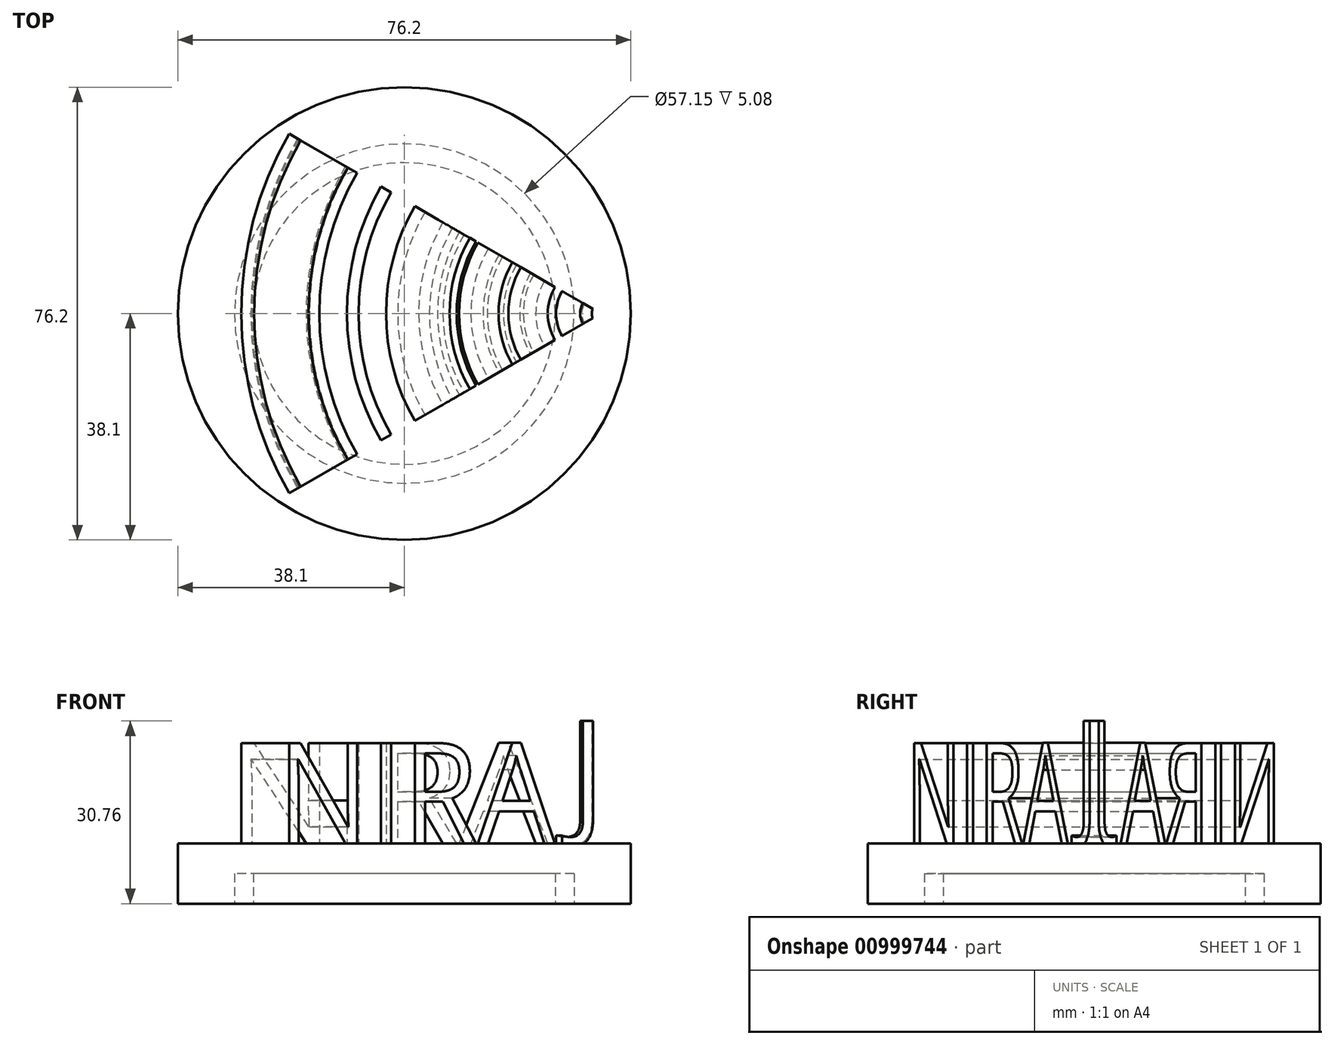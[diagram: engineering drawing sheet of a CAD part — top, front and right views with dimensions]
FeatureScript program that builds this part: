
annotation { "Feature Type Name" : "Feature", "Feature Type Description" : "" }
export const myFeature = defineFeature(function(context is Context, id is Id, definition is map)
    precondition{}
    {
        {
            var Q0;
            Q0=qCreatedBy(makeId("Top.planeOp"),FACE);
            var sketch = newSketch(context, id + "F0", { "sketchPlane" : qUnion([Q0])});
            skCircle(sketch, "E0", {"center": v(0, 0) * mm, "radius": 25.4 * mm});
            skCircle(sketch, "E1", {"center": v(0, 0) * mm, "radius": 28.58 * mm});
            skCircle(sketch, "E2", {"center": v(0, 0) * mm, "radius": 38.1 * mm});
            skSolve(sketch);
        }
        {
            var Q0;
            Q0=makeQuery(id+"F0.imprint","IMPRINT",FACE,{"disambiguationData":[TD([[makeQuery(id+"F0.imprint","IMPRINT",EDGE,{"derivedFrom":sQuery(id+"F0.wireOp",EDGE,"E1")}),-1.0]])]});
            var Q1;
            Q1=makeQuery(id+"F0.imprint","IMPRINT",FACE,{"disambiguationData":[TD([[makeQuery(id+"F0.imprint","IMPRINT",EDGE,{"derivedFrom":sQuery(id+"F0.wireOp",EDGE,"E0")}),-1.0]])]});
            var Q2;
            Q2=makeQuery(id+"F0.imprint","IMPRINT",FACE,{"disambiguationData":[TD([[makeQuery(id+"F0.imprint","IMPRINT",EDGE,{"derivedFrom":sQuery(id+"F0.wireOp",EDGE,"E0")}),1.0]])]});
            extrude(context, id + "F1", {"entities" : qUnion([Q0, Q1, Q2]), "depth" : 10.16 * mm, "offsetDistance" : 25.4 * mm});
        }
        {
            var Q0;
            Q0=makeQuery(id+"F0.imprint","IMPRINT",FACE,{"disambiguationData":[TD([[makeQuery(id+"F0.imprint","IMPRINT",EDGE,{"derivedFrom":sQuery(id+"F0.wireOp",EDGE,"E0")}),-1.0]])]});
            extrude(context, id + "F2", {"entities" : qUnion([Q0]), "operationType" : NewBodyOperationType.REMOVE, "depth" : 5.08 * mm, "offsetDistance" : 25.4 * mm});
        }
        {
            var Q0;
            Q0=qCreatedBy(makeId("Front.planeOp"),FACE);
            var sketch = newSketch(context, id + "F3", { "sketchPlane" : qUnion([Q0])});
            skText(sketch, "E3", { "text": "NIRAJ", "fontName": "OpenSans-Regular.ttf"});
            const initialGuessF3  = {"E3": [-0.02978, 0.01016, 1, 0, 0.017]};
            skSetInitialGuess(sketch, initialGuessF3);
            skSolve(sketch);
        }
        {
            var Q0;
            Q0=qCreatedBy(makeId("Front.planeOp"),FACE);
            var sketch = newSketch(context, id + "F4", { "sketchPlane" : qUnion([Q0])});
            skText(sketch, "E4", { "text": "NIRAJ", "fontName": "OpenSans-Regular.ttf"});
            const initialGuessF4  = {"E4": [-0.02654, 0.0139, 1, 0, 0.017]};
            skSetInitialGuess(sketch, initialGuessF4);
            skSolve(sketch);
        }
        {
            var Q0;
            Q0=makeQuery(id+"F3.imprint","IMPRINT",FACE,{"disambiguationData":[TD([[makeQuery(id+"F3.imprint","IMPRINT",EDGE,{"derivedFrom":sQuery(id+"F3.wireOp",EDGE,"E3.sketch_text.stroke-0")}),-1.0]])]});
            var Q1;
            Q1=makeQuery(id+"F3.imprint","IMPRINT",FACE,{"disambiguationData":[TD([[makeQuery(id+"F3.imprint","IMPRINT",EDGE,{"derivedFrom":sQuery(id+"F3.wireOp",EDGE,"E3.sketch_text.stroke-15")}),-1.0]])]});
            var Q2;
            Q2=makeQuery(id+"F3.imprint","IMPRINT",FACE,{"disambiguationData":[TD([[makeQuery(id+"F3.imprint","IMPRINT",EDGE,{"derivedFrom":sQuery(id+"F3.wireOp",EDGE,"E3.sketch_text.stroke-19")}),-1.0]])]});
            var Q3;
            Q3=makeQuery(id+"F3.imprint","IMPRINT",FACE,{"disambiguationData":[TD([[makeQuery(id+"F3.imprint","IMPRINT",EDGE,{"derivedFrom":sQuery(id+"F3.wireOp",EDGE,"E3.sketch_text.stroke-37")}),-1.0]])]});
            var Q4;
            Q4=makeQuery(id+"F4.imprint","IMPRINT",FACE,{"disambiguationData":[TD([[makeQuery(id+"F4.imprint","IMPRINT",EDGE,{"derivedFrom":sQuery(id+"F4.wireOp",EDGE,"E4.sketch_text.stroke-50")}),-1.0]])]});
            var Q5;
            Q5=sQuery(id+"F4.wireOp",EDGE,"E4.sketch_text.right");
            revolve(context, id + "F5", {"operationType" : NewBodyOperationType.ADD, "surfaceOperationType" : NewSurfaceOperationType.NEW, "entities" : qUnion([Q0, Q1, Q2, Q3, Q4]), "axis" : qUnion([Q5]), "revolveType" : RevolveType.SYMMETRIC, "angle" : 60 * degree});
        }
    });
